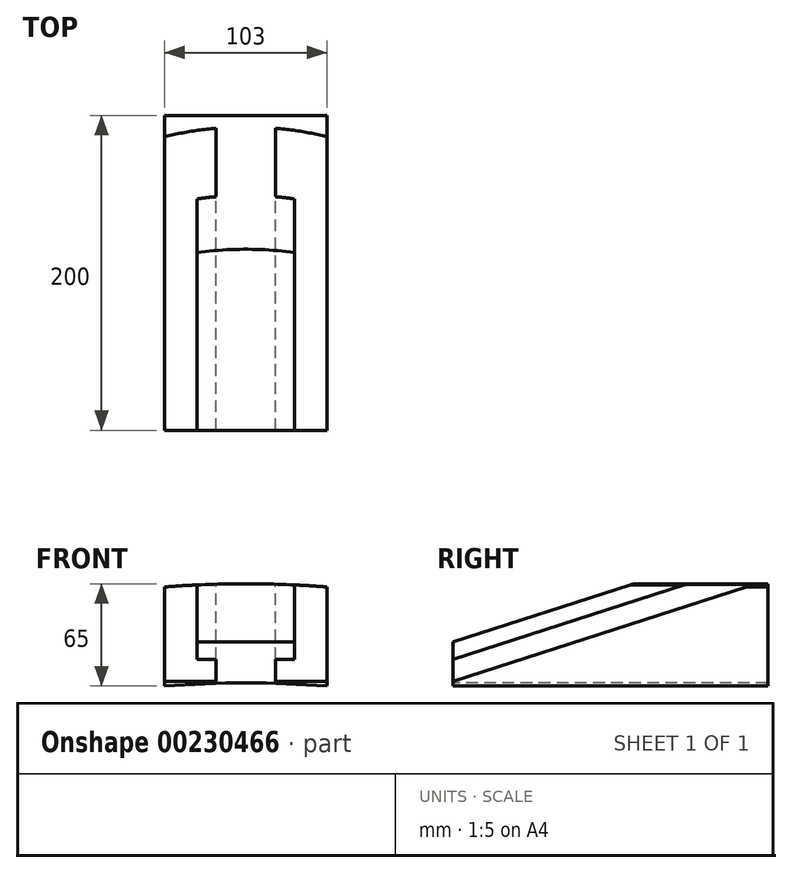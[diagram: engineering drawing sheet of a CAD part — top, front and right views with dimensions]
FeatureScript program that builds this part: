
annotation { "Feature Type Name" : "Feature", "Feature Type Description" : "" }
export const myFeature = defineFeature(function(context is Context, id is Id, definition is map)
    precondition{}
    {
        {
            var Q0;
            Q0=qCreatedBy(makeId("Right.planeOp"),FACE);
            var sketch = newSketch(context, id + "F0", { "sketchPlane" : qUnion([Q0])});
            skLineSegment(sketch, "E0", {"start": v(0, 0) * mm, "end": v(200, 0) * mm});
            skLineSegment(sketch, "E1", {"start": v(200, 0) * mm, "end": v(200, 65) * mm});
            skLineSegment(sketch, "E2", {"start": v(115, 65) * mm, "end": v(0, 28) * mm});
            skLineSegment(sketch, "E3", {"start": v(0, 28) * mm, "end": v(0, 17) * mm});
            skLineSegment(sketch, "E4", {"start": v(0, 17) * mm, "end": v(0, 3) * mm});
            skLineSegment(sketch, "E5", {"start": v(0, 3) * mm, "end": v(0, 0) * mm});
            skLineSegment(sketch, "E6", {"start": v(115, 65) * mm, "end": v(200, 65) * mm});
            skLineSegment(sketch, "E7", {"start": v(0, 17) * mm, "end": v(149.19, 65) * mm});
            skLineSegment(sketch, "E8", {"start": v(0, 3) * mm, "end": v(192.7, 65) * mm});
            skSolve(sketch);
        }
        {
            var Q0;
            Q0=makeQuery(id+"F0.imprint","IMPRINT",FACE,{"disambiguationData":[TD([[makeQuery(id+"F0.imprint","IMPRINT",EDGE,{"derivedFrom":sQuery(id+"F0.wireOp",EDGE,"E0")}),1.0]])]});
            extrude(context, id + "F1", {"entities" : qUnion([Q0]), "endBound" : BoundingType.SYMMETRIC, "depth" : 103 * mm});
        }
        {
            var Q0;
            Q0=makeQuery(id+"F0.imprint","IMPRINT",FACE,{"disambiguationData":[TD([[makeQuery(id+"F0.imprint","IMPRINT",EDGE,{"derivedFrom":sQuery(id+"F0.wireOp",EDGE,"E4")}),1.0]])]});
            extrude(context, id + "F2", {"entities" : qUnion([Q0]), "operationType" : NewBodyOperationType.ADD, "endBound" : BoundingType.SYMMETRIC, "depth" : 38 * mm});
        }
        {
            var Q0;
            {var subQ0=sQuery(id+"F0.wireOp",EDGE,"E2");Q0=makeQuery(id+"F0.imprint","IMPRINT",FACE,{"disambiguationData":[TD([[makeQuery(id+"F0.imprint","IMPRINT",EDGE,{"derivedFrom":subQ0}),1.0]])]});}
            extrude(context, id + "F3", {"entities" : qUnion([Q0]), "operationType" : NewBodyOperationType.ADD, "endBound" : BoundingType.SYMMETRIC, "depth" : 62 * mm});
        }
        {
            var Q0;
            Q0=qCreatedBy(makeId("Front.planeOp"),FACE);
            var sketch = newSketch(context, id + "F4", { "sketchPlane" : qUnion([Q0])});
            skLineSegment(sketch, "E9", {"start": v(0, 0) * mm, "end": v(-51.5, 0) * mm});
            skLineSegment(sketch, "E10", {"start": v(0, 0) * mm, "end": v(0, 2) * mm});
            skLineSegment(sketch, "E11", {"start": v(0, 0) * mm, "end": v(51.5, 0) * mm});
            skArc(sketch, "E12", {"start": v(51.5, 0) * mm, "mid": v(0, 2) * mm, "end": v(-51.5, 0) * mm});
            skSolve(sketch);
        }
        {
            var Q0;
            Q0 = qSketchRegion(id + "F4", true);
            extrude(context, id + "F5", {"entities" : qUnion([Q0]), "operationType" : NewBodyOperationType.REMOVE, "oppositeDirection" : true, "depth" : 200 * mm});
        }
        {
            var Q0;
            Q0=qCreatedBy(makeId("Front.planeOp"),FACE);
            var sketch = newSketch(context, id + "F6", { "sketchPlane" : qUnion([Q0])});
            skLineSegment(sketch, "E13", {"start": v(0, 0) * mm, "end": v(0, 63) * mm});
            skLineSegment(sketch, "E14", {"start": v(0, 63) * mm, "end": v(-51.5, 63) * mm});
            skLineSegment(sketch, "E15", {"start": v(0, 63) * mm, "end": v(51.5, 63) * mm});
            skLineSegment(sketch, "E16", {"start": v(0, 63) * mm, "end": v(0, 65) * mm});
            skArc(sketch, "E17", {"start": v(51.5, 63) * mm, "mid": v(0, 65) * mm, "end": v(-51.5, 63) * mm});
            skLineSegment(sketch, "E18", {"start": v(-51.5, 63) * mm, "end": v(-51.5, 65) * mm});
            skLineSegment(sketch, "E19", {"start": v(51.5, 63) * mm, "end": v(51.5, 65) * mm});
            skLineSegment(sketch, "E20", {"start": v(-51.5, 65) * mm, "end": v(51.5, 65) * mm});
            skSolve(sketch);
        }
        {
            var Q0;
            {var subQ0=sQuery(id+"F6.wireOp",EDGE,"E19");Q0=makeQuery(id+"F6.imprint","IMPRINT",FACE,{"disambiguationData":[TD([[makeQuery(id+"F6.imprint","IMPRINT",EDGE,{"derivedFrom":subQ0}),1.0]])]});}
            var Q1;
            {var subQ0=sQuery(id+"F6.wireOp",EDGE,"E18");Q1=makeQuery(id+"F6.imprint","IMPRINT",FACE,{"disambiguationData":[TD([[makeQuery(id+"F6.imprint","IMPRINT",EDGE,{"derivedFrom":subQ0}),-1.0]])]});}
            extrude(context, id + "F7", {"entities" : qUnion([Q0, Q1]), "operationType" : NewBodyOperationType.REMOVE, "oppositeDirection" : true, "depth" : 200 * mm});
        }
    });
